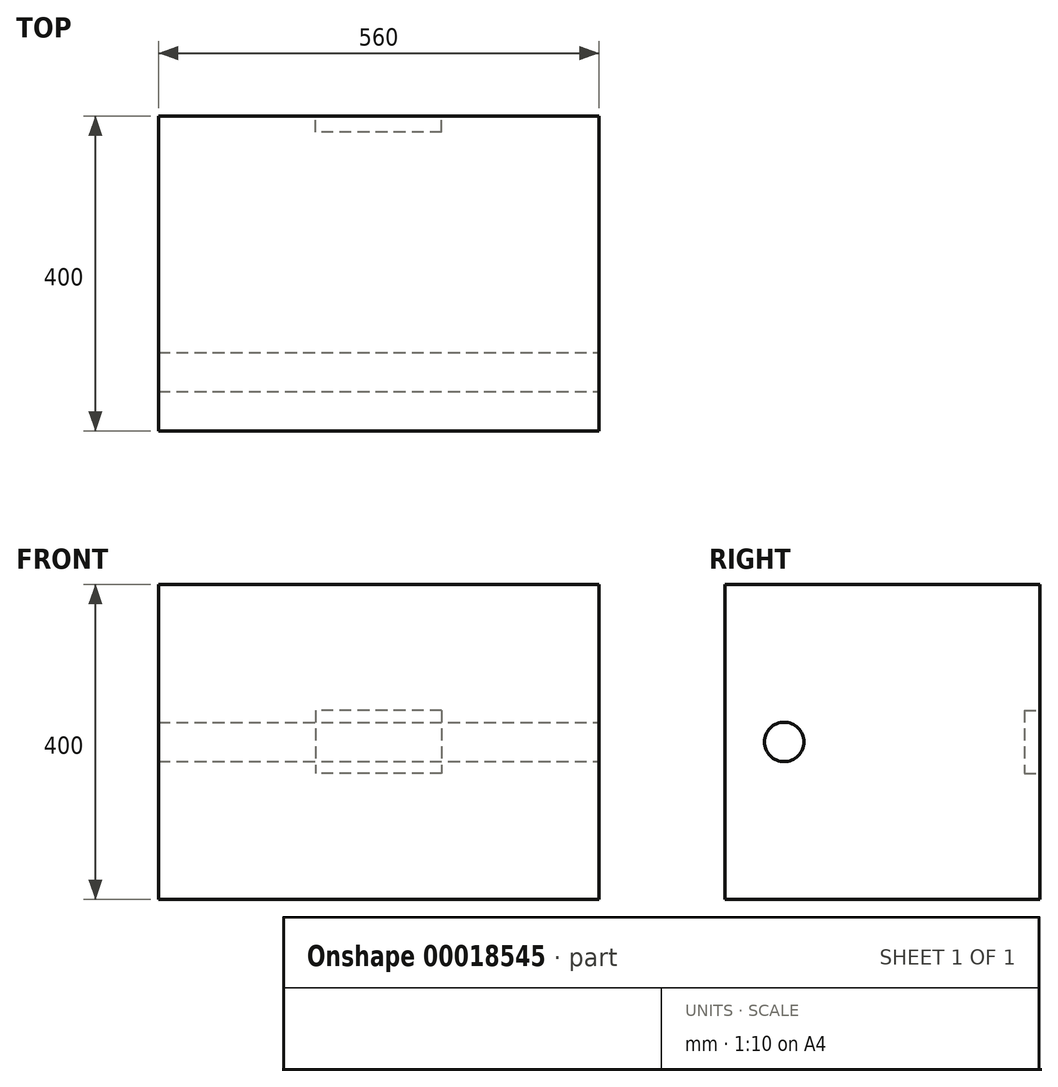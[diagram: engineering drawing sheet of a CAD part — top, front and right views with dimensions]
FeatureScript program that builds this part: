
annotation { "Feature Type Name" : "Feature", "Feature Type Description" : "" }
export const myFeature = defineFeature(function(context is Context, id is Id, definition is map)
    precondition{}
    {
        {
            var Q0;
            Q0=qCreatedBy(makeId("Front.planeOp"),FACE);
            var sketch = newSketch(context, id + "F0", { "sketchPlane" : qUnion([Q0])});
            skLineSegment(sketch, "E0.bottom", {"start": v(-264.46, 200) * mm, "end": v(295.54, 200) * mm});
            skLineSegment(sketch, "E0.top", {"start": v(-264.46, -200) * mm, "end": v(295.54, -200) * mm});
            skLineSegment(sketch, "E0.left", {"start": v(-264.46, 200) * mm, "end": v(-264.46, -200) * mm});
            skLineSegment(sketch, "E0.right", {"start": v(295.54, 200) * mm, "end": v(295.54, -200) * mm});
            skSolve(sketch);
        }
        {
            var Q0;
            Q0=makeQuery(id+"F0.imprint","IMPRINT",FACE,{"disambiguationData":[TD([[makeQuery(id+"F0.imprint","IMPRINT",EDGE,{"derivedFrom":sQuery(id+"F0.wireOp",EDGE,"E0.bottom")}),-1.0]])]});
            extrude(context, id + "F1", {"entities" : qUnion([Q0]), "oppositeDirection" : true, "depth" : 400 * mm});
        }
        {
            var Q0;
            Q0=makeQuery(id+"F1.opExtrude","CAP_FACE",FACE,{"disambiguationData":[OSD([sQuery(id+"F0.wireOp",EDGE,"E0.bottom"),sQuery(id+"F0.wireOp",EDGE,"E0.top"),sQuery(id+"F0.wireOp",EDGE,"E0.left"),sQuery(id+"F0.wireOp",EDGE,"E0.right")])],"isStart":false});
            var sketch = newSketch(context, id + "F2", { "sketchPlane" : qUnion([Q0])});
            skLineSegment(sketch, "E1.bottom", {"start": v(-95.54, 40) * mm, "end": v(64.46, 40) * mm});
            skLineSegment(sketch, "E1.top", {"start": v(-95.54, -40) * mm, "end": v(64.46, -40) * mm});
            skLineSegment(sketch, "E1.left", {"start": v(-95.54, 40) * mm, "end": v(-95.54, -40) * mm});
            skLineSegment(sketch, "E1.right", {"start": v(64.46, 40) * mm, "end": v(64.46, -40) * mm});
            skSolve(sketch);
        }
        {
            var Q0;
            Q0=makeQuery(id+"F2.imprint","IMPRINT",FACE,{"disambiguationData":[TD([[makeQuery(id+"F2.imprint","IMPRINT",EDGE,{"derivedFrom":sQuery(id+"F2.wireOp",EDGE,"E1.bottom")}),-1.0]])]});
            extrude(context, id + "F3", {"entities" : qUnion([Q0]), "operationType" : NewBodyOperationType.REMOVE, "oppositeDirection" : true, "depth" : 20 * mm});
        }
        {
            var Q0;
            Q0=makeQuery(id+"F1.opExtrude","SWEPT_FACE",FACE,{"disambiguationData":[OSD([sQuery(id+"F0.wireOp",EDGE,"E0.right")])]});
            var sketch = newSketch(context, id + "F4", { "sketchPlane" : qUnion([Q0])});
            skCircle(sketch, "E2", {"center": v(75, 0) * mm, "radius": 25 * mm});
            skSolve(sketch);
        }
        {
            var Q0;
            Q0=makeQuery(id+"F4.imprint","IMPRINT",FACE,{"disambiguationData":[TD([[makeQuery(id+"F4.imprint","IMPRINT",EDGE,{"derivedFrom":sQuery(id+"F4.wireOp",EDGE,"E2")}),1.0]])]});
            extrude(context, id + "F5", {"entities" : qUnion([Q0]), "endBound" : BoundingType.UP_TO_NEXT, "oppositeDirection" : true, "depth" : 25 * mm});
        }
    });
